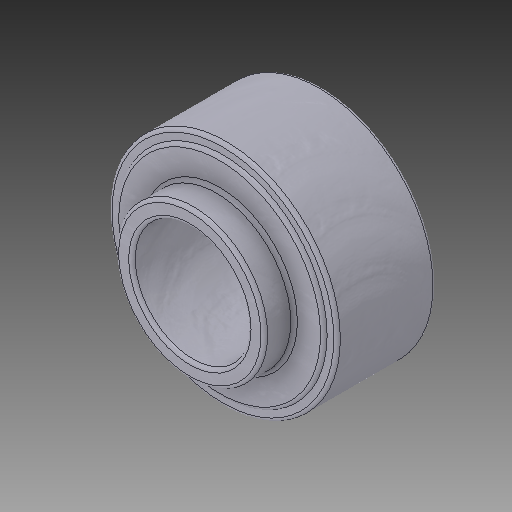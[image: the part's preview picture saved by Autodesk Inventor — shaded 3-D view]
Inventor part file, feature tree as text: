
AUTODESK INVENTOR PART (.ipt)
format: ipt  version: 2019 (Build 230136000, 136)  size: 223,232 bytes
history: native  units: in
note: dims shown in document units (in); Inventor stores cm internally (conversion verified against a paired STEP export)
features: sketch x6, other x3
ambient origin geometry x8: Origin, YZ Plane, XZ Plane, XY Plane, X Axis, Y Axis, Z Axis, Center Point
bodies: Solid1 (feature_tree)
feature tree (9):
  other  "project flange bearing part2_MIR1.ipt"
  other  "Solid1::project flange bearing part2_MIR1.ipt"
  other  "TaggingFeature1"
  sketch  "Sketch1"  dims[d0=0.3937in]
  sketch  "Sketch2"
  sketch  "Sketch3"
  sketch  "Sketch4"
  sketch  "Sketch5"
  sketch  "Sketch6"
